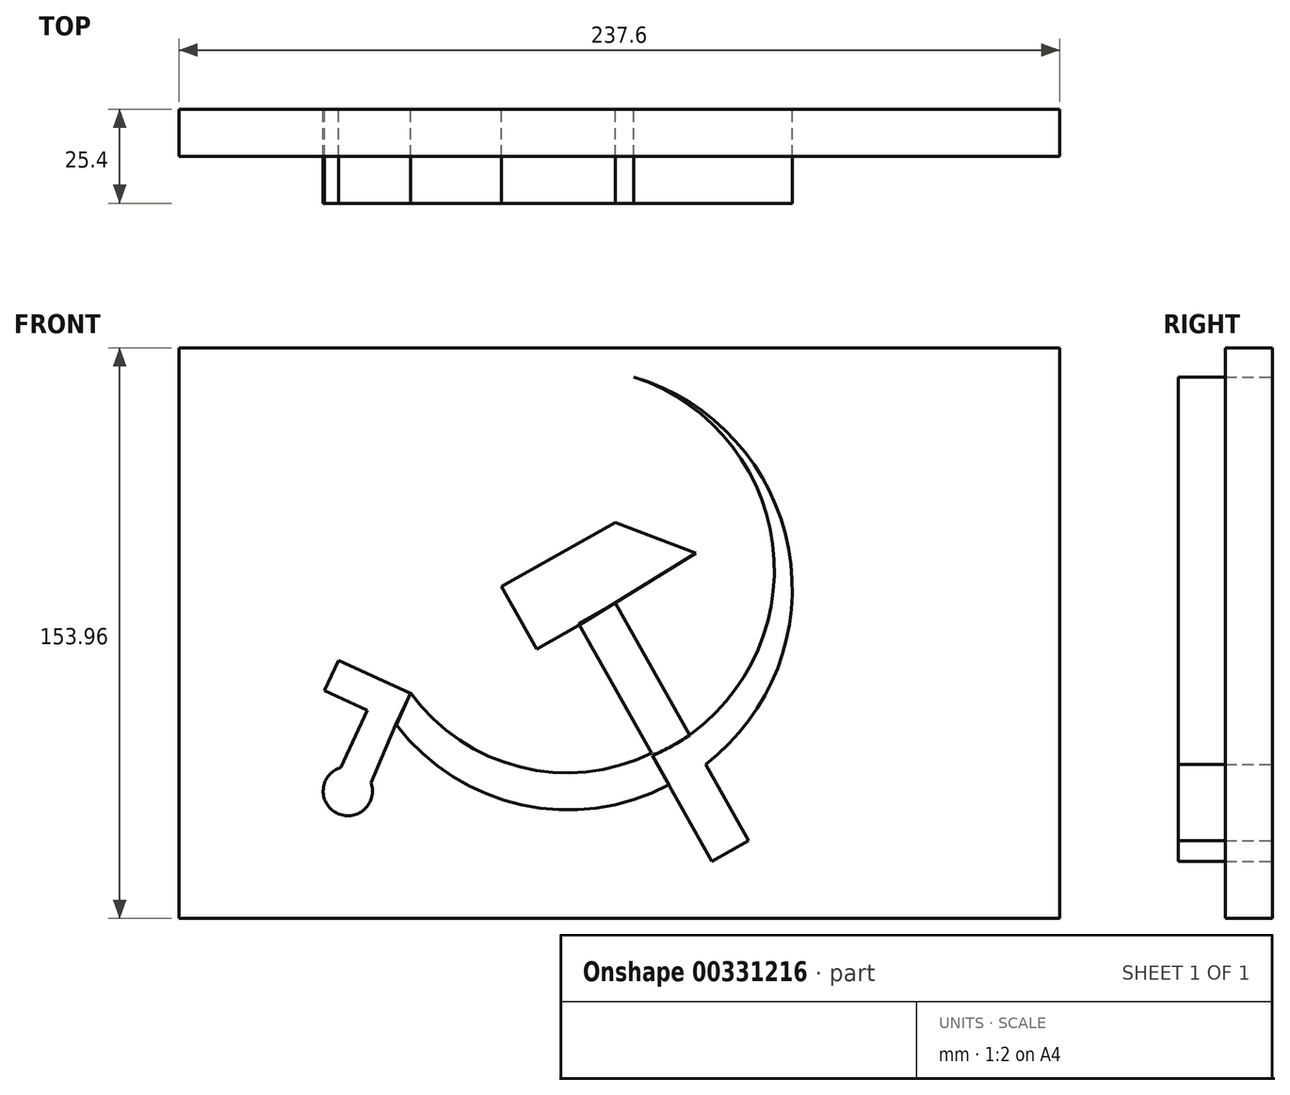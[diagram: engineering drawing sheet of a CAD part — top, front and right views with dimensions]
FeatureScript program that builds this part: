
annotation { "Feature Type Name" : "Feature", "Feature Type Description" : "" }
export const myFeature = defineFeature(function(context is Context, id is Id, definition is map)
    precondition{}
    {
        {
            var Q0;
            Q0=qCreatedBy(makeId("Front.planeOp"),FACE);
            var sketch = newSketch(context, id + "F0", { "sketchPlane" : qUnion([Q0])});
            skArc(sketch, "E0", {"start": v(-71.43, -15.42) * mm, "mid": v(-72.65, -27.72) * mm, "end": v(-63.35, -19.58) * mm});
            skLineSegment(sketch, "E1", {"start": v(-71.43, -15.42) * mm, "end": v(-64.33, 0) * mm});
            skLineSegment(sketch, "E2", {"start": v(-63.35, -19.58) * mm, "end": v(-56.75, -3.93) * mm});
            skLineSegment(sketch, "E3", {"start": v(-56.75, -3.93) * mm, "end": v(-64.33, 0) * mm});
            skLineSegment(sketch, "E4", {"start": v(-64.33, 0) * mm, "end": v(-75.84, 5.3) * mm});
            skLineSegment(sketch, "E5", {"start": v(-75.84, 5.3) * mm, "end": v(-72.09, 13.47) * mm});
            skLineSegment(sketch, "E6", {"start": v(-72.09, 13.47) * mm, "end": v(-52.62, 4.52) * mm});
            skLineSegment(sketch, "E7", {"start": v(-52.62, 4.52) * mm, "end": v(-56.75, -3.93) * mm});
            skArc(sketch, "E8", {"start": v(-56.11, -4.1) * mm, "mid": v(47.35, 14.22) * mm, "end": v(-25.23, 90.2) * mm});
            skArc(sketch, "E9", {"start": v(-52.62, 4.52) * mm, "mid": v(42.87, 21.2) * mm, "end": v(-25.23, 90.2) * mm});
            skLineSegment(sketch, "E10", {"start": v(28.65, -40.74) * mm, "end": v(-7.2, 23.02) * mm});
            skLineSegment(sketch, "E11", {"start": v(-7.2, 23.02) * mm, "end": v(-18.68, 16.56) * mm});
            skLineSegment(sketch, "E12", {"start": v(-18.68, 16.56) * mm, "end": v(-28.13, 33.36) * mm});
            skLineSegment(sketch, "E13", {"start": v(-28.13, 33.36) * mm, "end": v(2.6, 50.64) * mm});
            skLineSegment(sketch, "E14", {"start": v(2.6, 50.64) * mm, "end": v(24.3, 42.47) * mm});
            skLineSegment(sketch, "E15", {"start": v(24.3, 42.47) * mm, "end": v(-7.2, 23.02) * mm});
            skLineSegment(sketch, "E16", {"start": v(28.65, -40.74) * mm, "end": v(38.51, -35.2) * mm});
            skLineSegment(sketch, "E17", {"start": v(38.51, -35.2) * mm, "end": v(2.6, 28.67) * mm});
            skLineSegment(sketch, "E18", {"start": v(-7.2, 23.02) * mm, "end": v(12.65, -12.28) * mm});
            skLineSegment(sketch, "E19", {"start": v(2.6, 28.67) * mm, "end": v(22.5, -6.7) * mm});
            skLineSegment(sketch, "E20", {"start": v(22.5, -6.7) * mm, "end": v(12.65, -12.28) * mm});
            skArc(sketch, "E21", {"start": v(-52.62, 4.52) * mm, "mid": v(-22.78, -14.74) * mm, "end": v(12.65, -12.28) * mm});
            skArc(sketch, "E22", {"start": v(-56.11, -4.1) * mm, "mid": v(-22.36, -25.53) * mm, "end": v(17.3, -20.57) * mm});
            skSolve(sketch);
        }
        {
            var Q0;
            Q0=qCreatedBy(makeId("Front.planeOp"),FACE);
            var sketch = newSketch(context, id + "F1", { "sketchPlane" : qUnion([Q0])});
            skArc(sketch, "E23", {"start": v(-56.53, -3.97) * mm, "mid": v(-22.67, -25.52) * mm, "end": v(17.1, -20.08) * mm});
            skLineSegment(sketch, "E24", {"start": v(-56.53, -3.97) * mm, "end": v(-52.7, 4.72) * mm});
            skArc(sketch, "E25", {"start": v(-52.7, 4.72) * mm, "mid": v(-23.16, -15.3) * mm, "end": v(12.34, -11.6) * mm});
            skLineSegment(sketch, "E26", {"start": v(12.34, -11.6) * mm, "end": v(17.1, -20.08) * mm});
            skLineSegment(sketch, "E27", {"start": v(12.34, -11.6) * mm, "end": v(-7.32, 23.38) * mm});
            skLineSegment(sketch, "E28", {"start": v(-7.32, 23.38) * mm, "end": v(2.59, 28.95) * mm});
            skLineSegment(sketch, "E29", {"start": v(2.59, 28.95) * mm, "end": v(22.6, -6.68) * mm});
            skArc(sketch, "E30", {"start": v(12.34, -12.28) * mm, "mid": v(17.62, -9.74) * mm, "end": v(22.6, -6.68) * mm});
            skSolve(sketch);
        }
        {
            var Q0;
            Q0=makeQuery(id+"F0.imprint","IMPRINT",FACE,{"disambiguationData":[TD([[makeQuery(id+"F0.imprint","IMPRINT",EDGE,{"derivedFrom":sQuery(id+"F0.wireOp",EDGE,"E3")}),-1.0]])]});
            var Q1;
            Q1=makeQuery(id+"F0.imprint","IMPRINT",FACE,{"disambiguationData":[TD([[makeQuery(id+"F0.imprint","IMPRINT",EDGE,{"derivedFrom":sQuery(id+"F0.wireOp",EDGE,"E0")}),1.0]])]});
            var Q2;
            {var subQ3=sQuery(id+"F1.wireOp",EDGE,"E23");Q2=makeQuery(id+"F1.imprint","IMPRINT",FACE,{"disambiguationData":[TD([[makeQuery(id+"F1.imprint","IMPRINT",EDGE,{"derivedFrom":subQ3}),1.0]])]});}
            var Q3;
            {var subQ1=sQuery(id+"F1.wireOp",EDGE,"E27");Q3=makeQuery(id+"F1.imprint","IMPRINT",FACE,{"disambiguationData":[TD([[makeQuery(id+"F1.imprint","IMPRINT",EDGE,{"derivedFrom":subQ1}),-1.0]])]});}
            var Q4;
            {var subQ5=sQuery(id+"F0.wireOp",EDGE,"E16");Q4=makeQuery(id+"F0.imprint","IMPRINT",FACE,{"disambiguationData":[TD([[makeQuery(id+"F0.imprint","IMPRINT",EDGE,{"derivedFrom":subQ5}),1.0]])]});}
            var Q5;
            {var subQ1=sQuery(id+"F0.wireOp",EDGE,"E8");var subQ3=sQuery(id+"F0.wireOp",EDGE,"E17");var subQ4=makeQuery(id+"F0.imprint","INTERSECT",VERTEX,{"derivedFrom":[subQ1,subQ3]});Q5=makeQuery(id+"F0.imprint","IMPRINT",FACE,{"disambiguationData":[TD([[makeQuery(id+"F0.imprint","IMPRINT",EDGE,{"disambiguationData":[TD([[subQ4,1.0]])],"derivedFrom":subQ1}),1.0]])]});}
            var Q6;
            {var subQ0=sQuery(id+"F0.wireOp",EDGE,"E9");var subQ1=sQuery(id+"F0.wireOp",EDGE,"E8");var subQ2=makeQuery(id+"F0.imprint","INTERSECT",VERTEX,{"disambiguationData":[OD(1.0)],"derivedFrom":[subQ1,subQ0]});Q6=makeQuery(id+"F0.imprint","IMPRINT",FACE,{"disambiguationData":[TD([[makeQuery(id+"F0.imprint","IMPRINT",EDGE,{"disambiguationData":[TD([[subQ2,1.0]])],"derivedFrom":subQ1}),1.0]])]});}
            var Q7;
            Q7=makeQuery(id+"F0.imprint","IMPRINT",FACE,{"disambiguationData":[TD([[makeQuery(id+"F0.imprint","IMPRINT",EDGE,{"derivedFrom":sQuery(id+"F0.wireOp",EDGE,"E11")}),-1.0]])]});
            extrude(context, id + "F2", {"entities" : qUnion([Q0, Q1, Q2, Q3, Q4, Q5, Q6, Q7]), "depth" : 25.4 * mm});
        }
        {
            var Q0;
            Q0=qCreatedBy(makeId("Front.planeOp"),FACE);
            var sketch = newSketch(context, id + "F3", { "sketchPlane" : qUnion([Q0])});
            skLineSegment(sketch, "E31", {"start": v(-115.15, 97.8) * mm, "end": v(-115.15, -56.16) * mm});
            skLineSegment(sketch, "E32", {"start": v(-115.15, -56.16) * mm, "end": v(122.45, -56.16) * mm});
            skLineSegment(sketch, "E33", {"start": v(122.45, -56.16) * mm, "end": v(122.45, 97.8) * mm});
            skLineSegment(sketch, "E34", {"start": v(-115.15, 97.8) * mm, "end": v(122.45, 97.8) * mm});
            skSolve(sketch);
        }
        {
            var Q0;
            Q0=makeQuery(id+"F3.imprint","IMPRINT",FACE,{"disambiguationData":[TD([[makeQuery(id+"F3.imprint","IMPRINT",EDGE,{"derivedFrom":sQuery(id+"F3.wireOp",EDGE,"E31")}),1.0]])]});
            extrude(context, id + "F4", {"entities" : qUnion([Q0]), "depth" : 12.7 * mm});
        }
    });
